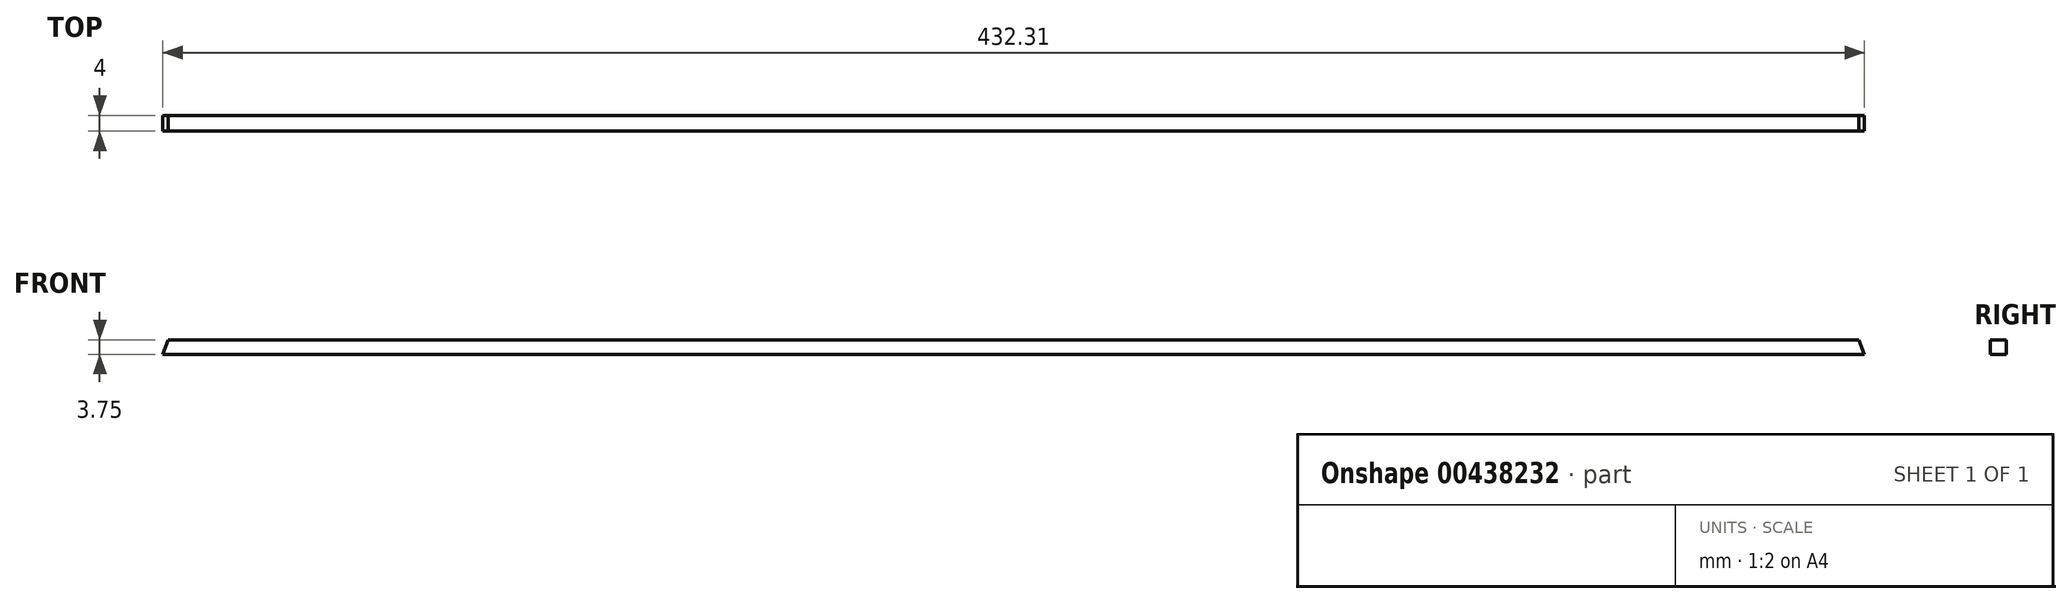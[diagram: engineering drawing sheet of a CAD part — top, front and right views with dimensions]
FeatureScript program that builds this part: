
annotation { "Feature Type Name" : "Feature", "Feature Type Description" : "" }
export const myFeature = defineFeature(function(context is Context, id is Id, definition is map)
    precondition{}
    {
        {
            var Q0;
            Q0=qCreatedBy(makeId("Front.planeOp"),FACE);
            var sketch = newSketch(context, id + "F0", { "sketchPlane" : qUnion([Q0])});
            skLineSegment(sketch, "E0", {"start": v(-21.75, 4.6) * mm, "end": v(-20.35, 8.35) * mm});
            skLineSegment(sketch, "E1", {"start": v(-20.35, 8.35) * mm, "end": v(409.16, 8.35) * mm});
            skLineSegment(sketch, "E2", {"start": v(409.16, 8.35) * mm, "end": v(410.56, 4.6) * mm});
            skLineSegment(sketch, "E3", {"start": v(410.56, 4.6) * mm, "end": v(-21.75, 4.6) * mm});
            skSolve(sketch);
        }
        {
            var Q0;
            Q0=makeQuery(id+"F0.imprint","IMPRINT",FACE,{"disambiguationData":[TD([[makeQuery(id+"F0.imprint","IMPRINT",EDGE,{"derivedFrom":sQuery(id+"F0.wireOp",EDGE,"E0")}),-1.0]])]});
            extrude(context, id + "F1", {"entities" : qUnion([Q0]), "depth" : 4 * mm, "offsetDistance" : 25.4 * mm});
        }
    });
